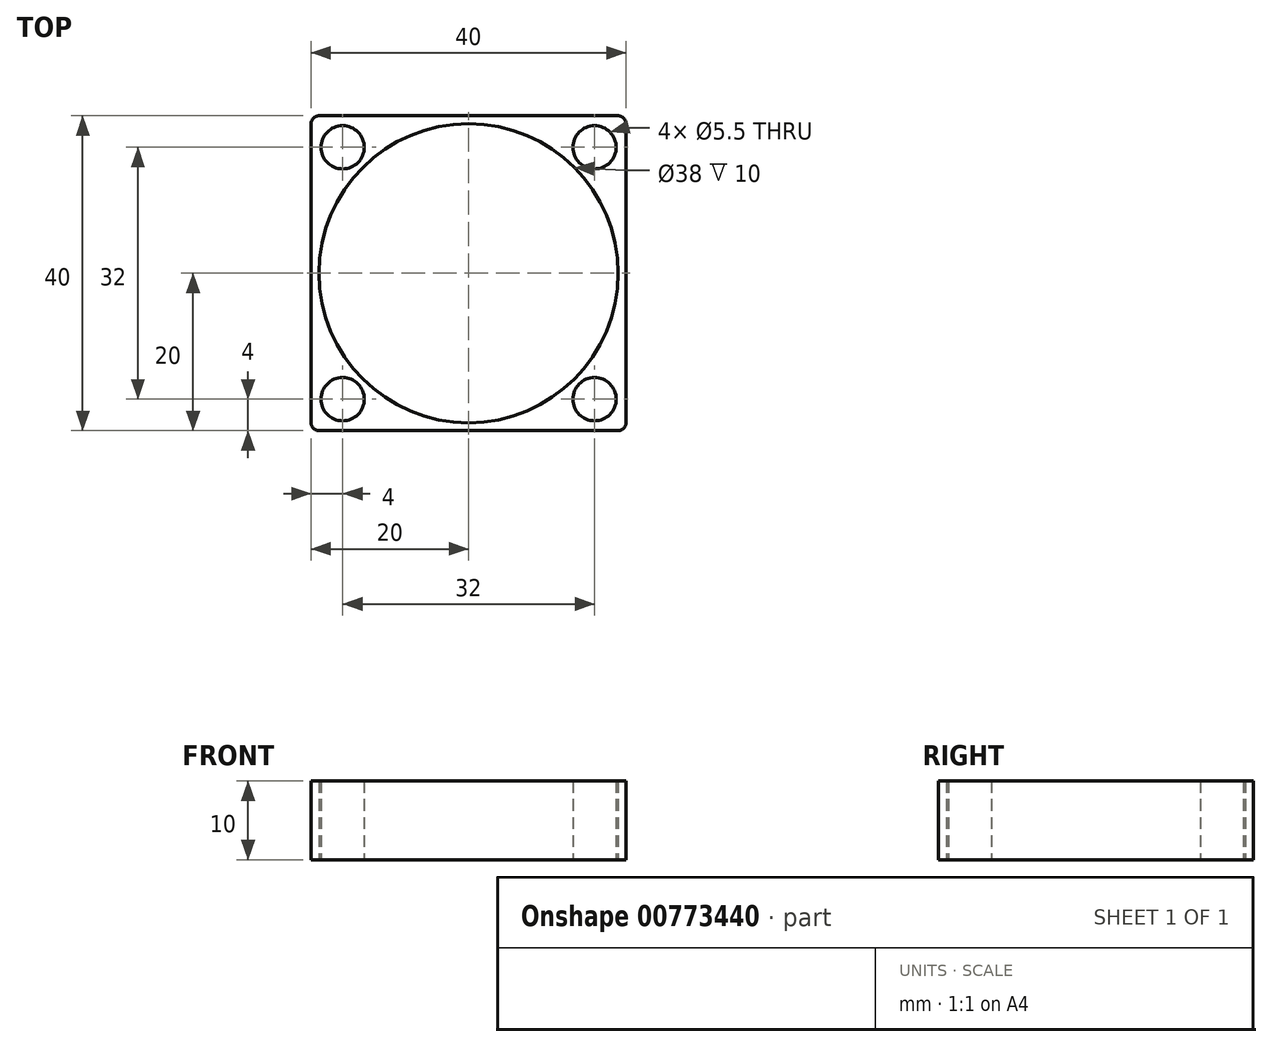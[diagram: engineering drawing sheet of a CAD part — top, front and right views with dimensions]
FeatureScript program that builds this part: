
annotation { "Feature Type Name" : "Feature", "Feature Type Description" : "" }
export const myFeature = defineFeature(function(context is Context, id is Id, definition is map)
    precondition{}
    {
        {
            var Q0;
            Q0=qCreatedBy(makeId("Top.planeOp"),FACE);
            var sketch = newSketch(context, id + "F0", { "sketchPlane" : qUnion([Q0])});
            skLineSegment(sketch, "E0.bottom", {"start": v(19, -20) * mm, "end": v(-19, -20) * mm});
            skLineSegment(sketch, "E0.top", {"start": v(19, 20) * mm, "end": v(-19, 20) * mm});
            skLineSegment(sketch, "E0.left", {"start": v(20, -19) * mm, "end": v(20, 19) * mm});
            skLineSegment(sketch, "E0.right", {"start": v(-20, -19) * mm, "end": v(-20, 19) * mm});
            skPoint(sketch, "E0.middle", {"position": v(0, 0) * mm});
            skPoint(sketch, "E1.visualSharp", {"position": v(-20, 20) * mm});
            skArc(sketch, "E1.filletArc", {"start": v(-19, 20) * mm, "mid": v(-19.7, 19.7) * mm, "end": v(-20, 19) * mm});
            skPoint(sketch, "E2.visualSharp", {"position": v(20, 20) * mm});
            skArc(sketch, "E2.filletArc", {"start": v(20, 19) * mm, "mid": v(19.7, 19.7) * mm, "end": v(19, 20) * mm});
            skPoint(sketch, "E3.visualSharp", {"position": v(20, -20) * mm});
            skArc(sketch, "E3.filletArc", {"start": v(19, -20) * mm, "mid": v(19.7, -19.7) * mm, "end": v(20, -19) * mm});
            skPoint(sketch, "E4.visualSharp", {"position": v(-20, -20) * mm});
            skArc(sketch, "E4.filletArc", {"start": v(-20, -19) * mm, "mid": v(-19.7, -19.7) * mm, "end": v(-19, -20) * mm});
            skLineSegment(sketch, "E5.bottom", {"start": v(16, -16) * mm, "end": v(-16, -16) * mm, "construction": true});
            skLineSegment(sketch, "E5.top", {"start": v(16, 16) * mm, "end": v(-16, 16) * mm, "construction": true});
            skLineSegment(sketch, "E5.left", {"start": v(16, -16) * mm, "end": v(16, 16) * mm, "construction": true});
            skLineSegment(sketch, "E5.right", {"start": v(-16, -16) * mm, "end": v(-16, 16) * mm, "construction": true});
            skPoint(sketch, "E6", {"position": v(-16, 16) * mm});
            skPoint(sketch, "E7", {"position": v(16, 16) * mm});
            skPoint(sketch, "E8", {"position": v(16, -16) * mm});
            skPoint(sketch, "E9", {"position": v(-16, -16) * mm});
            skCircle(sketch, "E10", {"center": v(0, 0) * mm, "radius": 19 * mm});
            skSolve(sketch);
        }
        {
            var Q0;
            Q0 = qSketchRegion(id + "F0", true);
            extrude(context, id + "F1", {"entities" : qUnion([Q0]), "depth" : 10 * mm, "offsetDistance" : 25 * mm});
        }
        {
            var Q0;
            Q0=sQuery(id+"F0.wireOp",VERTEX,"E6");
            var Q1;
            Q1=sQuery(id+"F0.wireOp",VERTEX,"E7");
            var Q2;
            Q2=sQuery(id+"F0.wireOp",VERTEX,"E8");
            var Q3;
            Q3=sQuery(id+"F0.wireOp",VERTEX,"E9");
            var Q4;
            Q4=makeQuery(id+"F1.opExtrude","SWEPT_BODY",BODY,{"disambiguationData":[OSD([sQuery(id+"F0.wireOp",EDGE,"E0.bottom"),sQuery(id+"F0.wireOp",EDGE,"E0.top"),sQuery(id+"F0.wireOp",EDGE,"E0.left"),sQuery(id+"F0.wireOp",EDGE,"E0.right"),sQuery(id+"F0.wireOp",EDGE,"E1.filletArc"),sQuery(id+"F0.wireOp",EDGE,"E2.filletArc"),sQuery(id+"F0.wireOp",EDGE,"E3.filletArc"),sQuery(id+"F0.wireOp",EDGE,"E4.filletArc"),sQuery(id+"F0.wireOp",EDGE,"E10")])]});
            hole(context, id + "F2", {"style" : HoleStyle.SIMPLE, "endStyle" : HoleEndStyle.THROUGH, "oppositeDirection" : true, "standardTappedOrClearance" : lookupTablePath({ "fit" : "Normal", "standard" : "ISO", "size" : "M5", "type" : "Clearance" }), "standardBlindInLast" : lookupTablePath({ "fit" : "Normal", "standard" : "ISO", "size" : "M5", "type" : "Clearance" }), "holeDiameter" : 5.5 * mm, "majorDiameter" : 5 * mm, "tappedDepth" : 12 * mm, "tapClearance" : 3, "startFromSketch" : true, "locations" : qUnion([Q0, Q1, Q2, Q3]), "scope" : qUnion([Q4])});
        }
    });
